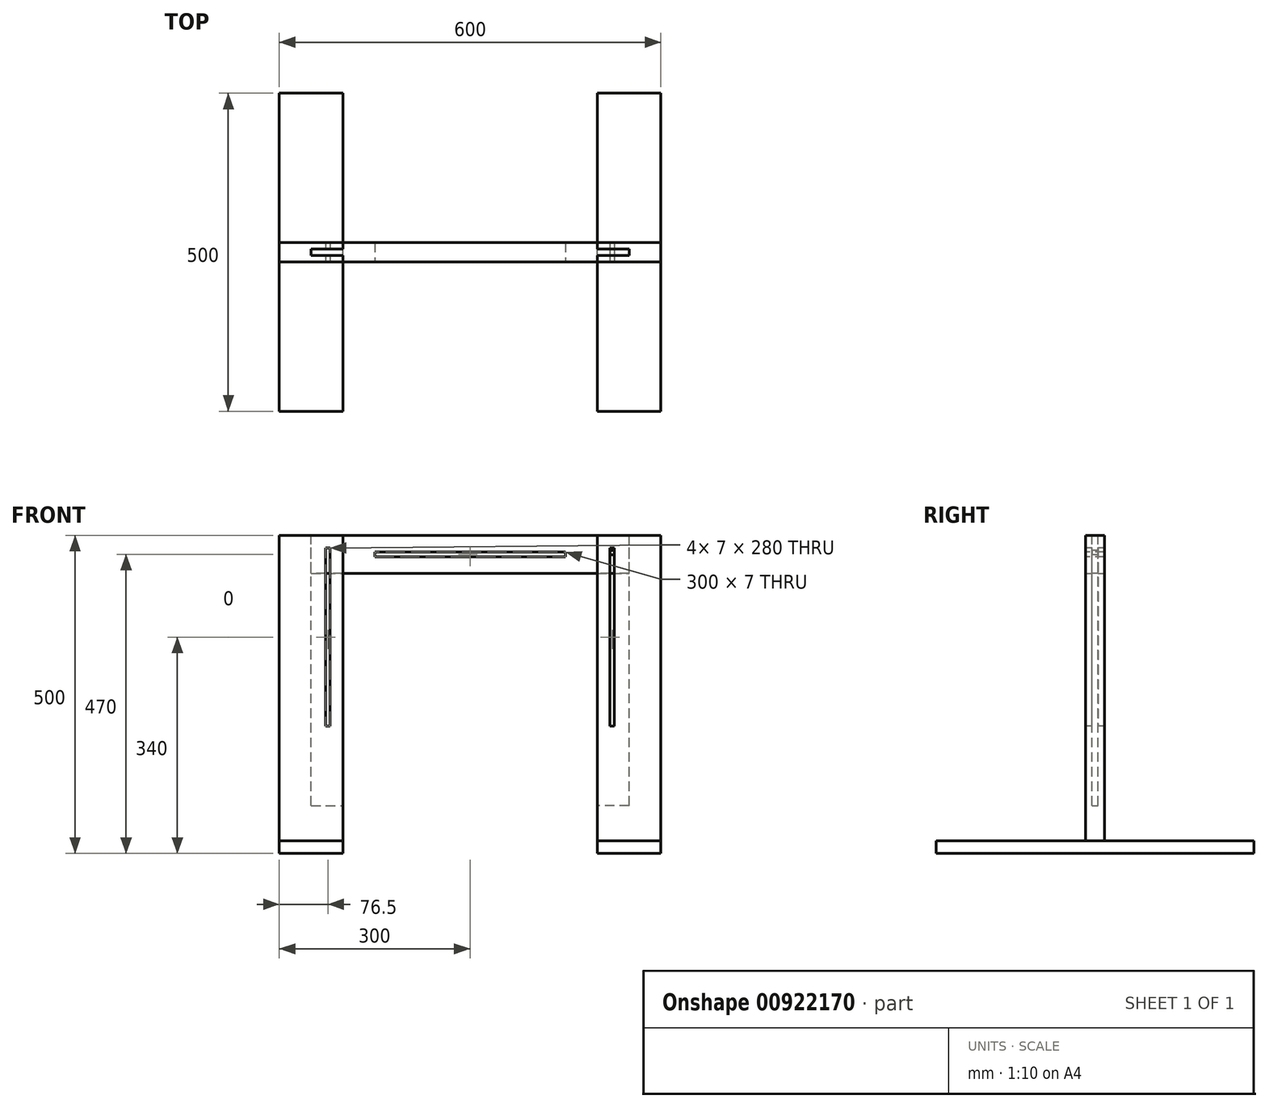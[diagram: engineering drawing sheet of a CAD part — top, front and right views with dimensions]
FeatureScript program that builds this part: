
annotation { "Feature Type Name" : "Feature", "Feature Type Description" : "" }
export const myFeature = defineFeature(function(context is Context, id is Id, definition is map)
    precondition{}
    {
        {
            var Q0;
            Q0=qCreatedBy(makeId("Front.planeOp"),FACE);
            var sketch = newSketch(context, id + "F0", { "sketchPlane" : qUnion([Q0])});
            skLineSegment(sketch, "E0", {"start": v(0, 0) * mm, "end": v(-200, 0) * mm});
            skLineSegment(sketch, "E1", {"start": v(-200, 0) * mm, "end": v(200, 0) * mm});
            skLineSegment(sketch, "E2", {"start": v(0, 0) * mm, "end": v(0, 75.68) * mm, "construction": true});
            skLineSegment(sketch, "E3", {"start": v(-200, 0) * mm, "end": v(-200, 20) * mm});
            skLineSegment(sketch, "E4", {"start": v(-200, 20) * mm, "end": v(-300, 20) * mm});
            skLineSegment(sketch, "E5", {"start": v(-300, 20) * mm, "end": v(-300, 0) * mm});
            skPoint(sketch, "E6.MirrorCS.start.orphan", {"position": v(-200, 0) * mm});
            skPoint(sketch, "E7.MirrorCS.end.orphan", {"position": v(-300, 0) * mm});
            skLineSegment(sketch, "E8", {"start": v(-200, 0) * mm, "end": v(-300, 0) * mm});
            skPoint(sketch, "E9.start.orphan", {"position": v(200, 0) * mm});
            skLineSegment(sketch, "E10.MirrorCS", {"start": v(200, 20) * mm, "end": v(300, 20) * mm});
            skLineSegment(sketch, "E11.MirrorCS", {"start": v(200, 0) * mm, "end": v(200, 20) * mm});
            skLineSegment(sketch, "E12.MirrorCS", {"start": v(200, 0) * mm, "end": v(300, 0) * mm});
            skLineSegment(sketch, "E13.MirrorCS", {"start": v(300, 20) * mm, "end": v(300, 0) * mm});
            skSolve(sketch);
        }
        {
            var Q0;
            Q0 = qSketchRegion(id + "F0", true);
            extrude(context, id + "F1", {"entities" : qUnion([Q0]), "endBound" : BoundingType.SYMMETRIC, "depth" : 500 * mm, "offsetDistance" : 25 * mm});
        }
        {
            var Q0;
            Q0=qCreatedBy(makeId("Front.planeOp"),FACE);
            var sketch = newSketch(context, id + "F2", { "sketchPlane" : qUnion([Q0])});
            skLineSegment(sketch, "E14", {"start": v(-200, 0) * mm, "end": v(-299.98, 0) * mm});
            skLineSegment(sketch, "E15.0.1", {"start": v(-299.98, 0) * mm, "end": v(-299.98, 0) * mm});
            skLineSegment(sketch, "E15.0.5", {"start": v(-200, 0) * mm, "end": v(-200, 0) * mm});
            skLineSegment(sketch, "E16", {"start": v(-299.98, 0) * mm, "end": v(-299.98, 500) * mm});
            skLineSegment(sketch, "E17", {"start": v(-299.98, 500) * mm, "end": v(-200, 500) * mm});
            skLineSegment(sketch, "E18", {"start": v(-200, 500) * mm, "end": v(-200, 0) * mm});
            skLineSegment(sketch, "E19", {"start": v(0, 0) * mm, "end": v(0, 188.1) * mm, "construction": true});
            skLineSegment(sketch, "E20", {"start": v(0, 0) * mm, "end": v(-200, 0) * mm});
            skLineSegment(sketch, "E21.0.0", {"start": v(-300, 0) * mm, "end": v(-200, 0) * mm});
            skLineSegment(sketch, "E21.0.1", {"start": v(-200, 0) * mm, "end": v(-200, 20) * mm});
            skLineSegment(sketch, "E21.0.2", {"start": v(-200, 20) * mm, "end": v(-300, 20) * mm});
            skLineSegment(sketch, "E21.0.3", {"start": v(-300, 20) * mm, "end": v(-300, 0) * mm});
            skLineSegment(sketch, "E22", {"start": v(-299.98, 0) * mm, "end": v(-299.98, 305) * mm});
            skLineSegment(sketch, "E23", {"start": v(-200, 20) * mm, "end": v(-200, 229) * mm});
            skSolve(sketch);
        }
        {
            var Q0;
            {var subQ0=sQuery(id+"F2.wireOp",EDGE,"E17");Q0=makeQuery(id+"F2.imprint","IMPRINT",FACE,{"disambiguationData":[TD([[makeQuery(id+"F2.imprint","IMPRINT",EDGE,{"derivedFrom":subQ0}),-1.0]])]});}
            extrude(context, id + "F3", {"entities" : qUnion([Q0]), "endBound" : BoundingType.SYMMETRIC, "depth" : 30 * mm, "offsetDistance" : 25 * mm});
        }
        {
            var Q0;
            Q0=makeQuery(id+"F3.opExtrude","SWEPT_FACE",FACE,{"disambiguationData":[OSD([sQuery(id+"F2.wireOp",EDGE,"E17")])]});
            var sketch = newSketch(context, id + "F4", { "sketchPlane" : qUnion([Q0])});
            skLineSegment(sketch, "E24.0.0", {"start": v(-200, 15) * mm, "end": v(-299.98, 15) * mm});
            skLineSegment(sketch, "E24.0.1", {"start": v(-299.98, 15) * mm, "end": v(-299.98, -15) * mm});
            skLineSegment(sketch, "E24.0.2", {"start": v(-299.98, -15) * mm, "end": v(-200, -15) * mm});
            skLineSegment(sketch, "E24.0.3", {"start": v(-200, -15) * mm, "end": v(-200, 15) * mm});
            skLineSegment(sketch, "E25", {"start": v(-200, 0) * mm, "end": v(-250, 0) * mm});
            skPoint(sketch, "E25.endSnap0", {"position": v(-250, -15) * mm});
            skLineSegment(sketch, "E26", {"start": v(-250, 0) * mm, "end": v(-250, -5) * mm});
            skLineSegment(sketch, "E27", {"start": v(-250, -5) * mm, "end": v(-250, 5) * mm});
            skLineSegment(sketch, "E28", {"start": v(-250, 5) * mm, "end": v(-200, 5) * mm});
            skLineSegment(sketch, "E29", {"start": v(-200, 5) * mm, "end": v(-200, -5) * mm});
            skLineSegment(sketch, "E30", {"start": v(-200, -5) * mm, "end": v(-250, -5) * mm});
            skLineSegment(sketch, "E31", {"start": v(-250, -15) * mm, "end": v(-200, -15) * mm});
            skSolve(sketch);
        }
        {
            var Q0;
            {var subQ0=sQuery(id+"F4.wireOp",EDGE,"E25");Q0=makeQuery(id+"F4.imprint","IMPRINT",FACE,{"disambiguationData":[TD([[makeQuery(id+"F4.imprint","IMPRINT",EDGE,{"derivedFrom":subQ0}),1.0]])]});}
            var Q1;
            {var subQ0=sQuery(id+"F4.wireOp",EDGE,"E25");Q1=makeQuery(id+"F4.imprint","IMPRINT",FACE,{"disambiguationData":[TD([[makeQuery(id+"F4.imprint","IMPRINT",EDGE,{"derivedFrom":subQ0}),-1.0]])]});}
            extrude(context, id + "F5", {"entities" : qUnion([Q0, Q1]), "operationType" : NewBodyOperationType.REMOVE, "oppositeDirection" : true, "depth" : 425 * mm, "offsetDistance" : 25 * mm});
        }
        {
            var Q0;
            Q0=makeQuery(id+"F3.opExtrude","SWEPT_BODY",BODY,{"disambiguationData":[OSD([sQuery(id+"F2.wireOp",EDGE,"E16"),sQuery(id+"F2.wireOp",EDGE,"E17"),sQuery(id+"F2.wireOp",EDGE,"E18"),sQuery(id+"F2.wireOp",EDGE,"392abc95-a1c7-4a86-a4d4-d3f2c5f82420.0.0"),sQuery(id+"F2.wireOp",EDGE,"E15.0.1"),sQuery(id+"F2.wireOp",EDGE,"E15.0.5"),sQuery(id+"F2.wireOp",EDGE,"392abc95-a1c7-4a86-a4d4-d3f2c5f82420.0.6"),sQuery(id+"F2.wireOp",EDGE,"392abc95-a1c7-4a86-a4d4-d3f2c5f82420.0.7"),sQuery(id+"F2.wireOp",EDGE,"392abc95-a1c7-4a86-a4d4-d3f2c5f82420.0.8"),sQuery(id+"F2.wireOp",EDGE,"392abc95-a1c7-4a86-a4d4-d3f2c5f82420.0.9"),sQuery(id+"F2.wireOp",EDGE,"392abc95-a1c7-4a86-a4d4-d3f2c5f82420.0.10"),sQuery(id+"F2.wireOp",EDGE,"392abc95-a1c7-4a86-a4d4-d3f2c5f82420.0.11"),sQuery(id+"F2.wireOp",EDGE,"392abc95-a1c7-4a86-a4d4-d3f2c5f82420.0.12"),sQuery(id+"F2.wireOp",EDGE,"392abc95-a1c7-4a86-a4d4-d3f2c5f82420.0.13"),sQuery(id+"F2.wireOp",EDGE,"392abc95-a1c7-4a86-a4d4-d3f2c5f82420.0.14"),sQuery(id+"F2.wireOp",EDGE,"392abc95-a1c7-4a86-a4d4-d3f2c5f82420.0.15")])]});
            var Q1;
            Q1=qCreatedBy(makeId("Right.planeOp"),FACE);
            mirror(context, id + "F6", {"entities" : qUnion([Q0]), "mirrorPlane" : qUnion([Q1])});
        }
        {
            var Q0;
            Q0=makeQuery(id+"F3.opExtrude","CAP_FACE",FACE,{"disambiguationData":[OSD([sQuery(id+"F2.wireOp",EDGE,"E16"),sQuery(id+"F2.wireOp",EDGE,"E17"),sQuery(id+"F2.wireOp",EDGE,"E18"),sQuery(id+"F2.wireOp",EDGE,"392abc95-a1c7-4a86-a4d4-d3f2c5f82420.0.0"),sQuery(id+"F2.wireOp",EDGE,"E15.0.1"),sQuery(id+"F2.wireOp",EDGE,"E15.0.5"),sQuery(id+"F2.wireOp",EDGE,"392abc95-a1c7-4a86-a4d4-d3f2c5f82420.0.6"),sQuery(id+"F2.wireOp",EDGE,"392abc95-a1c7-4a86-a4d4-d3f2c5f82420.0.7"),sQuery(id+"F2.wireOp",EDGE,"392abc95-a1c7-4a86-a4d4-d3f2c5f82420.0.8"),sQuery(id+"F2.wireOp",EDGE,"392abc95-a1c7-4a86-a4d4-d3f2c5f82420.0.9"),sQuery(id+"F2.wireOp",EDGE,"392abc95-a1c7-4a86-a4d4-d3f2c5f82420.0.10"),sQuery(id+"F2.wireOp",EDGE,"392abc95-a1c7-4a86-a4d4-d3f2c5f82420.0.11"),sQuery(id+"F2.wireOp",EDGE,"392abc95-a1c7-4a86-a4d4-d3f2c5f82420.0.12"),sQuery(id+"F2.wireOp",EDGE,"392abc95-a1c7-4a86-a4d4-d3f2c5f82420.0.13"),sQuery(id+"F2.wireOp",EDGE,"392abc95-a1c7-4a86-a4d4-d3f2c5f82420.0.14"),sQuery(id+"F2.wireOp",EDGE,"392abc95-a1c7-4a86-a4d4-d3f2c5f82420.0.15")])],"isStart":false});
            var sketch = newSketch(context, id + "F7", { "sketchPlane" : qUnion([Q0])});
            skLineSegment(sketch, "E32.0.13", {"start": v(-200, 20) * mm, "end": v(-200, 500) * mm});
            skLineSegment(sketch, "E32.0.14", {"start": v(-200, 500) * mm, "end": v(-299.98, 500) * mm});
            skLineSegment(sketch, "E32.0.15", {"start": v(-299.98, 500) * mm, "end": v(-299.98, 500) * mm});
            skLineSegment(sketch, "E33", {"start": v(-200, 500) * mm, "end": v(-220, 500) * mm});
            skLineSegment(sketch, "E34", {"start": v(-220, 500) * mm, "end": v(-220, 480) * mm});
            skLineSegment(sketch, "E35", {"start": v(-220, 480) * mm, "end": v(-220, 200) * mm});
            skLineSegment(sketch, "E36", {"start": v(-220, 200) * mm, "end": v(-227, 200) * mm});
            skLineSegment(sketch, "E37", {"start": v(-227, 200) * mm, "end": v(-227, 480) * mm});
            skLineSegment(sketch, "E38", {"start": v(-227, 480) * mm, "end": v(-220, 480) * mm});
            skLineSegment(sketch, "E39.MirrorCS", {"start": v(220, 200) * mm, "end": v(227, 200) * mm});
            skLineSegment(sketch, "E40.MirrorCS", {"start": v(227, 200) * mm, "end": v(227, 480) * mm});
            skLineSegment(sketch, "E41.MirrorCS", {"start": v(220, 480) * mm, "end": v(220, 200) * mm});
            skLineSegment(sketch, "E42.MirrorCS", {"start": v(227, 480) * mm, "end": v(220, 480) * mm});
            skLineSegment(sketch, "E43", {"start": v(0, 0) * mm, "end": v(0, 179.02) * mm, "construction": true});
            skLineSegment(sketch, "E44", {"start": v(-220, 200) * mm, "end": v(-220, 0) * mm});
            skSolve(sketch);
        }
        {
            var Q0;
            Q0=makeQuery(id+"F7.imprint","IMPRINT",FACE,{"disambiguationData":[TD([[makeQuery(id+"F7.imprint","IMPRINT",EDGE,{"derivedFrom":sQuery(id+"F7.wireOp",EDGE,"E35")}),-1.0]])]});
            var Q1;
            Q1=makeQuery(id+"F7.imprint","IMPRINT",FACE,{"disambiguationData":[TD([[makeQuery(id+"F7.imprint","IMPRINT",EDGE,{"derivedFrom":sQuery(id+"F7.wireOp",EDGE,"E39.MirrorCS")}),1.0]])]});
            extrude(context, id + "F8", {"entities" : qUnion([Q0, Q1]), "operationType" : NewBodyOperationType.REMOVE, "oppositeDirection" : true, "depth" : 110 * mm, "offsetDistance" : 25 * mm});
        }
        {
            var Q0;
            Q0=makeQuery(id+"F3.opExtrude","SWEPT_FACE",FACE,{"disambiguationData":[OSD([sQuery(id+"F2.wireOp",EDGE,"E17")])]});
            var sketch = newSketch(context, id + "F9", { "sketchPlane" : qUnion([Q0])});
            skLineSegment(sketch, "E45", {"start": v(-200, -15) * mm, "end": v(-200, -5) * mm});
            skLineSegment(sketch, "E46", {"start": v(-200, -5) * mm, "end": v(-250, -5) * mm});
            skLineSegment(sketch, "E47", {"start": v(-250, -5) * mm, "end": v(-250, 5) * mm});
            skLineSegment(sketch, "E48", {"start": v(-250, 5) * mm, "end": v(-200, 5) * mm});
            skLineSegment(sketch, "E49", {"start": v(-200, 5) * mm, "end": v(-200, 15) * mm});
            skLineSegment(sketch, "E50.0.0", {"start": v(200, -5) * mm, "end": v(200, -15) * mm});
            skLineSegment(sketch, "E50.0.4", {"start": v(200, 15) * mm, "end": v(200, 5) * mm});
            skLineSegment(sketch, "E50.0.5", {"start": v(200, 5) * mm, "end": v(250, 5) * mm});
            skLineSegment(sketch, "E50.0.6", {"start": v(250, 5) * mm, "end": v(250, -5) * mm});
            skLineSegment(sketch, "E50.0.7", {"start": v(250, -5) * mm, "end": v(200, -5) * mm});
            skPoint(sketch, "E50.0.2.end.orphan", {"position": v(299.98, 15) * mm});
            skPoint(sketch, "E50.0.1.end.orphan", {"position": v(299.98, -15) * mm});
            skLineSegment(sketch, "E51", {"start": v(0, 0) * mm, "end": v(0, -15) * mm, "construction": true});
            skLineSegment(sketch, "E52", {"start": v(0, -15) * mm, "end": v(-200, -15) * mm});
            skLineSegment(sketch, "E53", {"start": v(0, 0) * mm, "end": v(0, 15) * mm, "construction": true});
            skLineSegment(sketch, "E54", {"start": v(0, 15) * mm, "end": v(-200, 15) * mm});
            skLineSegment(sketch, "E55", {"start": v(0, 15) * mm, "end": v(200, 15) * mm});
            skLineSegment(sketch, "E56", {"start": v(200, -15) * mm, "end": v(0, -15) * mm});
            skSolve(sketch);
        }
        {
            var Q0;
            Q0=makeQuery(id+"F9.imprint","IMPRINT",FACE,{"disambiguationData":[TD([[makeQuery(id+"F9.imprint","IMPRINT",EDGE,{"derivedFrom":sQuery(id+"F9.wireOp",EDGE,"E46")}),-1.0]])]});
            extrude(context, id + "F10", {"entities" : qUnion([Q0]), "oppositeDirection" : true, "depth" : 60 * mm, "offsetDistance" : 25 * mm});
        }
        {
            var Q0;
            Q0=makeQuery(id+"F10.opExtrude","SWEPT_FACE",FACE,{"disambiguationData":[OSD([sQuery(id+"F9.wireOp",EDGE,"E50.0.5")])]});
            var sketch = newSketch(context, id + "F11", { "sketchPlane" : qUnion([Q0])});
            skLineSegment(sketch, "E57.0.0", {"start": v(-200, 500) * mm, "end": v(-250, 500) * mm});
            skLineSegment(sketch, "E57.0.1", {"start": v(-250, 500) * mm, "end": v(-250, 440) * mm});
            skLineSegment(sketch, "E57.0.2", {"start": v(-250, 440) * mm, "end": v(-200, 440) * mm});
            skLineSegment(sketch, "E57.0.3", {"start": v(-200, 440) * mm, "end": v(-200, 500) * mm});
            skLineSegment(sketch, "E58", {"start": v(0, 0) * mm, "end": v(0, 185.23) * mm, "construction": true});
            skLineSegment(sketch, "E59.0", {"start": v(-227, 480) * mm, "end": v(-220, 480) * mm});
            skLineSegment(sketch, "E60", {"start": v(-200, 500) * mm, "end": v(-227, 500) * mm});
            skLineSegment(sketch, "E61", {"start": v(-227, 500) * mm, "end": v(-220, 500) * mm});
            skLineSegment(sketch, "E62", {"start": v(-220, 480) * mm, "end": v(-200, 480) * mm});
            skPoint(sketch, "E63.orphan", {"position": v(-225, 440) * mm});
            skLineSegment(sketch, "E64", {"start": v(-220, 480) * mm, "end": v(-227, 480) * mm});
            skLineSegment(sketch, "E65", {"start": v(-223.5, 480) * mm, "end": v(-223.5, 473) * mm});
            skCircle(sketch, "E66", {"center": v(-223.5, 473) * mm, "radius": 3.5 * mm});
            skCircle(sketch, "E67.MirrorC", {"center": v(223.5, 473) * mm, "radius": 3.5 * mm});
            skSolve(sketch);
        }
        {
            var Q0;
            Q0=makeQuery(id+"F11.imprint","IMPRINT",FACE,{"disambiguationData":[TD([[makeQuery(id+"F11.imprint","IMPRINT",EDGE,{"derivedFrom":sQuery(id+"F11.wireOp",EDGE,"E66")}),1.0]])]});
            var Q1;
            Q1=makeQuery(id+"F11.imprint","IMPRINT",FACE,{"disambiguationData":[TD([[makeQuery(id+"F11.imprint","IMPRINT",EDGE,{"derivedFrom":sQuery(id+"F11.wireOp",EDGE,"E67.MirrorC")}),-1.0]])]});
            extrude(context, id + "F12", {"entities" : qUnion([Q0, Q1]), "operationType" : NewBodyOperationType.REMOVE, "endBound" : BoundingType.SYMMETRIC, "depth" : 112 * mm, "offsetDistance" : 25 * mm});
        }
        {
            var Q0;
            Q0=makeQuery(id+"F10.opExtrude","SWEPT_FACE",FACE,{"disambiguationData":[OSD([sQuery(id+"F9.wireOp",EDGE,"E52"),sQuery(id+"F9.wireOp",EDGE,"E56")])]});
            var sketch = newSketch(context, id + "F13", { "sketchPlane" : qUnion([Q0])});
            skLineSegment(sketch, "E68.0.0", {"start": v(200, 500) * mm, "end": v(-200, 500) * mm});
            skLineSegment(sketch, "E68.0.1", {"start": v(-200, 500) * mm, "end": v(-200, 440) * mm});
            skLineSegment(sketch, "E68.0.2", {"start": v(-200, 440) * mm, "end": v(200, 440) * mm});
            skLineSegment(sketch, "E68.0.3", {"start": v(200, 440) * mm, "end": v(200, 500) * mm});
            skLineSegment(sketch, "E69", {"start": v(0, 500) * mm, "end": v(0, 440) * mm, "construction": true});
            skLineSegment(sketch, "E70", {"start": v(0, 470) * mm, "end": v(-150, 470) * mm, "construction": true});
            skLineSegment(sketch, "E71.0", {"start": v(-227, 480) * mm, "end": v(-220, 480) * mm});
            skLineSegment(sketch, "E72", {"start": v(-150, 470) * mm, "end": v(-150, 466.5) * mm});
            skLineSegment(sketch, "E73", {"start": v(-150, 466.5) * mm, "end": v(-150, 473.5) * mm});
            skLineSegment(sketch, "E74", {"start": v(-150, 473.5) * mm, "end": v(0, 473.5) * mm});
            skLineSegment(sketch, "E75", {"start": v(-150, 466.5) * mm, "end": v(0, 466.5) * mm});
            skLineSegment(sketch, "E76.MirrorCS", {"start": v(150, 466.5) * mm, "end": v(0, 466.5) * mm});
            skLineSegment(sketch, "E77.MirrorCS", {"start": v(150, 473.5) * mm, "end": v(0, 473.5) * mm});
            skLineSegment(sketch, "E78.MirrorCS", {"start": v(150, 466.5) * mm, "end": v(150, 473.5) * mm});
            skSolve(sketch);
        }
        {
            var Q0;
            {var subQ1=sQuery(id+"F13.wireOp",EDGE,"E74");Q0=makeQuery(id+"F13.imprint","IMPRINT",FACE,{"disambiguationData":[TD([[makeQuery(id+"F13.imprint","IMPRINT",EDGE,{"derivedFrom":subQ1}),-1.0]])]});}
            extrude(context, id + "F14", {"entities" : qUnion([Q0]), "operationType" : NewBodyOperationType.REMOVE, "oppositeDirection" : true, "depth" : 46 * mm, "offsetDistance" : 25 * mm});
        }
    });
